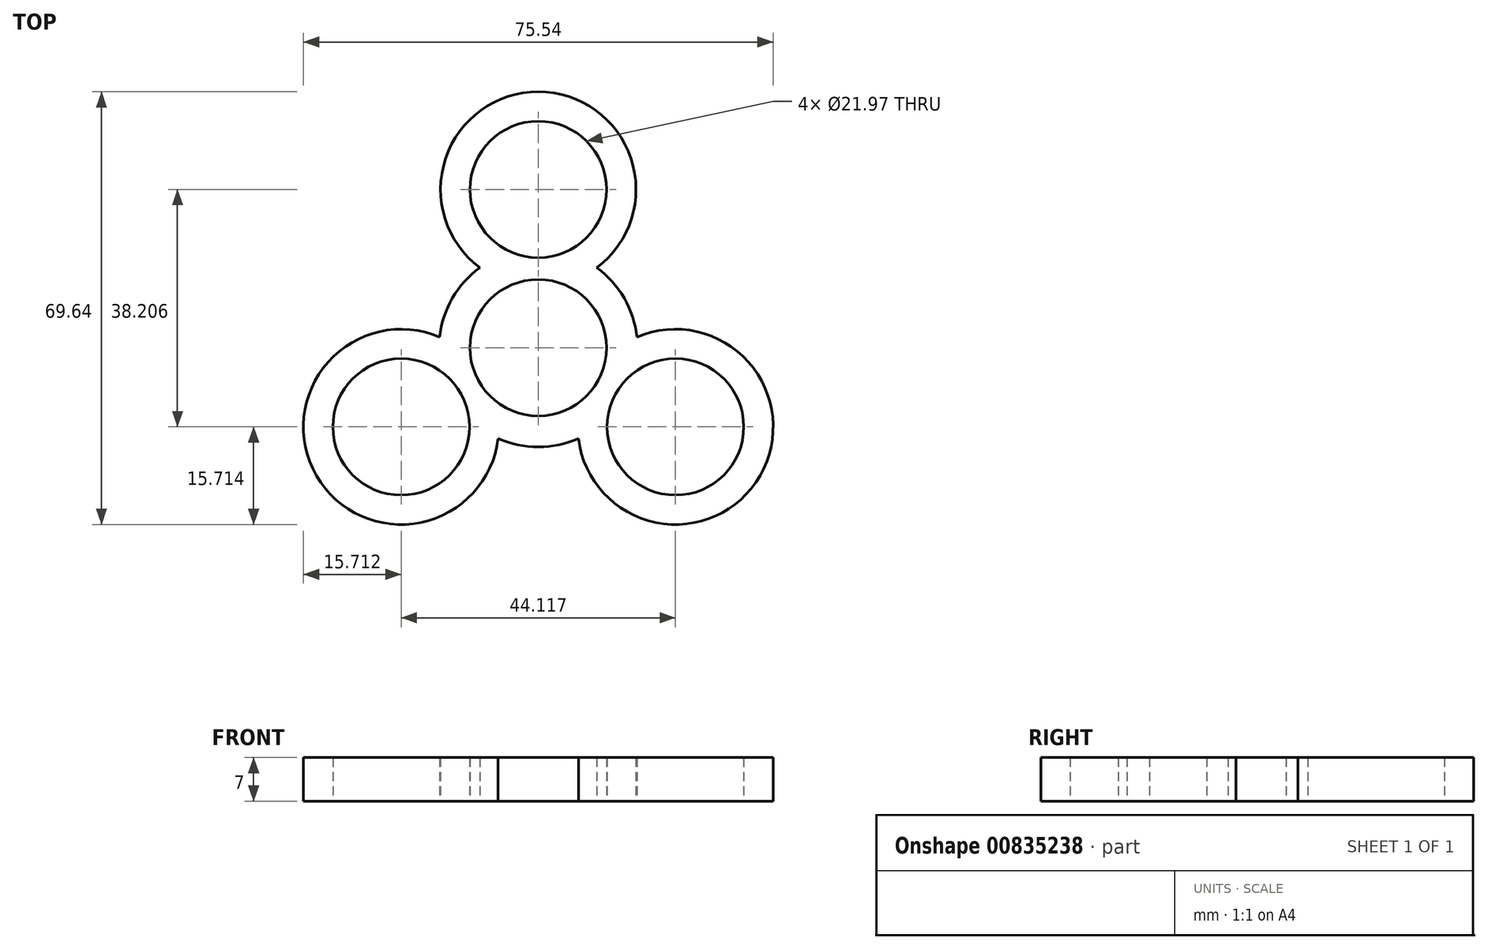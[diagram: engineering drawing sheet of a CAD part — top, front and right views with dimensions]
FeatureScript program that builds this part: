
annotation { "Feature Type Name" : "Feature", "Feature Type Description" : "" }
export const myFeature = defineFeature(function(context is Context, id is Id, definition is map)
    precondition{}
    {
        {
            var Q0;
            Q0=qCreatedBy(makeId("Top.planeOp"),FACE);
            var sketch = newSketch(context, id + "F0", { "sketchPlane" : qUnion([Q0])});
            skCircle(sketch, "E0", {"center": v(0, 0) * mm, "radius": 10.99 * mm});
            skCircle(sketch, "E1", {"center": v(0, 0) * mm, "radius": 25.47 * mm, "construction": true});
            skCircle(sketch, "E2", {"center": v(0, 25.47) * mm, "radius": 10.99 * mm});
            skCircle(sketch, "E3", {"center": v(-22.06, -12.74) * mm, "radius": 10.99 * mm});
            skCircle(sketch, "E4", {"center": v(22.06, -12.74) * mm, "radius": 10.99 * mm});
            skLineSegment(sketch, "E5.bottom", {"start": v(-57.15, 57.15) * mm, "end": v(57.15, 57.15) * mm, "construction": true});
            skLineSegment(sketch, "E5.top", {"start": v(-57.15, -57.15) * mm, "end": v(57.15, -57.15) * mm, "construction": true});
            skLineSegment(sketch, "E5.left", {"start": v(-57.15, 57.15) * mm, "end": v(-57.15, -57.15) * mm, "construction": true});
            skLineSegment(sketch, "E5.right", {"start": v(57.15, 57.15) * mm, "end": v(57.15, -57.15) * mm, "construction": true});
            skPoint(sketch, "E6", {"position": v(-57.15, 0) * mm});
            skPoint(sketch, "E7", {"position": v(0, 57.15) * mm});
            skArc(sketch, "E8", {"start": v(6.45, -14.59) * mm, "mid": v(35.67, -20.6) * mm, "end": v(15.86, 1.7) * mm});
            skArc(sketch, "E9", {"start": v(-15.86, 1.7) * mm, "mid": v(-35.67, -20.6) * mm, "end": v(-6.45, -14.59) * mm});
            skArc(sketch, "E10.trimOffspring", {"start": v(-9.4, 12.88) * mm, "mid": v(-13.82, 7.98) * mm, "end": v(-15.86, 1.7) * mm});
            skArc(sketch, "E11.trimOffspring", {"start": v(-6.45, -14.59) * mm, "mid": v(0, -15.95) * mm, "end": v(6.45, -14.59) * mm});
            skArc(sketch, "E12.trimOffspring", {"start": v(15.86, 1.7) * mm, "mid": v(13.82, 7.98) * mm, "end": v(9.4, 12.88) * mm});
            skArc(sketch, "E13.trimOffspring", {"start": v(9.4, 12.88) * mm, "mid": v(0, 41.19) * mm, "end": v(-9.4, 12.88) * mm});
            skSolve(sketch);
        }
        {
            var Q0;
            Q0 = qSketchRegion(id + "F0", true);
            extrude(context, id + "F1", {"entities" : qUnion([Q0]), "depth" : 7 * mm, "offsetDistance" : 25.4 * mm});
        }
    });
